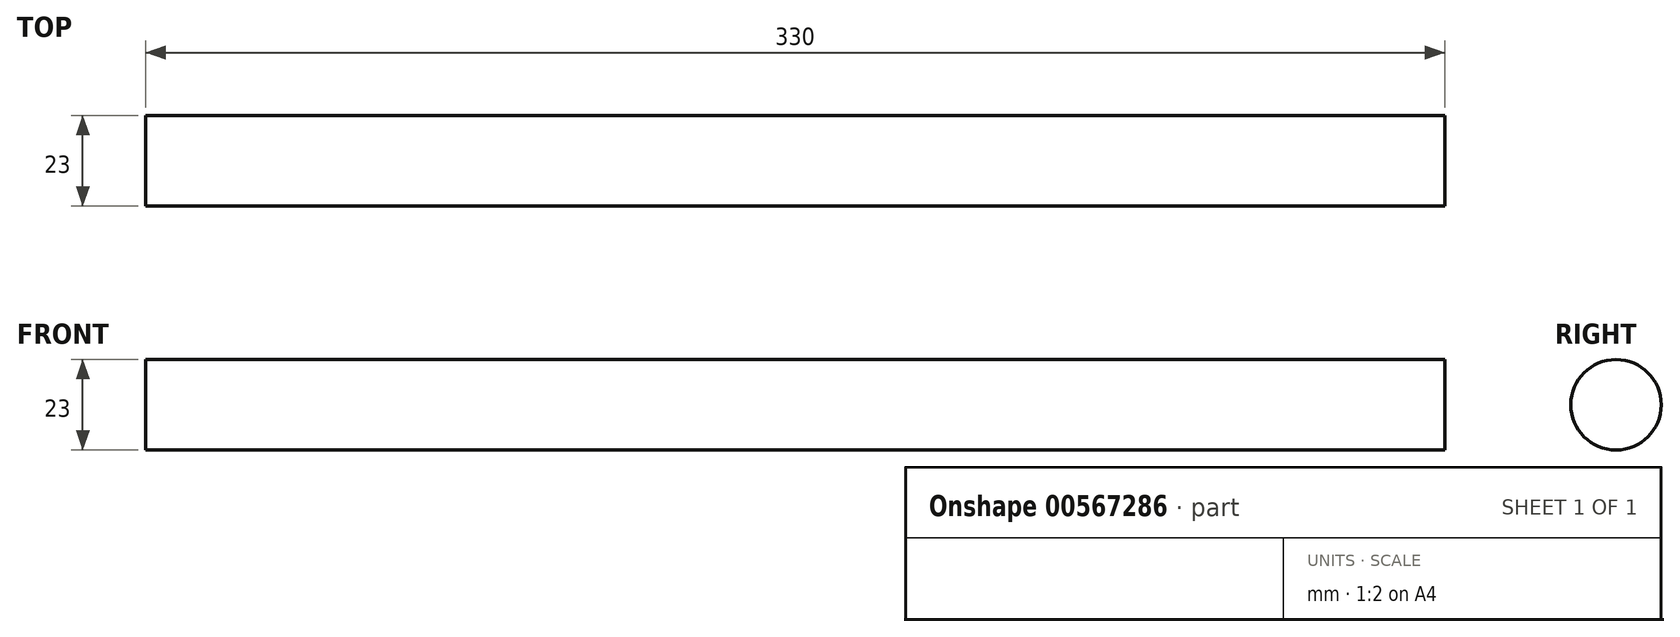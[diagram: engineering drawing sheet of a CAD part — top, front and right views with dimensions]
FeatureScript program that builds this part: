
annotation { "Feature Type Name" : "Feature", "Feature Type Description" : "" }
export const myFeature = defineFeature(function(context is Context, id is Id, definition is map)
    precondition{}
    {
        {
            var Q0;
            Q0=qCreatedBy(makeId("Right.planeOp"),FACE);
            var sketch = newSketch(context, id + "F0", { "sketchPlane" : qUnion([Q0])});
            skEllipse(sketch, "E0", {"center": v(-37.44, 52.62) * mm, "majorRadius": 11.5 * mm, "minorRadius": 11.5 * mm, "majorAxis": v(0, -1)});
            skSolve(sketch);
        }
        {
            var Q0;
            Q0=makeQuery(id+"F0.imprint","IMPRINT",FACE,{"disambiguationData":[TD([[makeQuery(id+"F0.imprint","IMPRINT",EDGE,{"derivedFrom":sQuery(id+"F0.wireOp",EDGE,"E0")}),1.0]])]});
            extrude(context, id + "F1", {"entities" : qUnion([Q0]), "depth" : 330 * mm, "offsetDistance" : 25 * mm});
        }
    });
